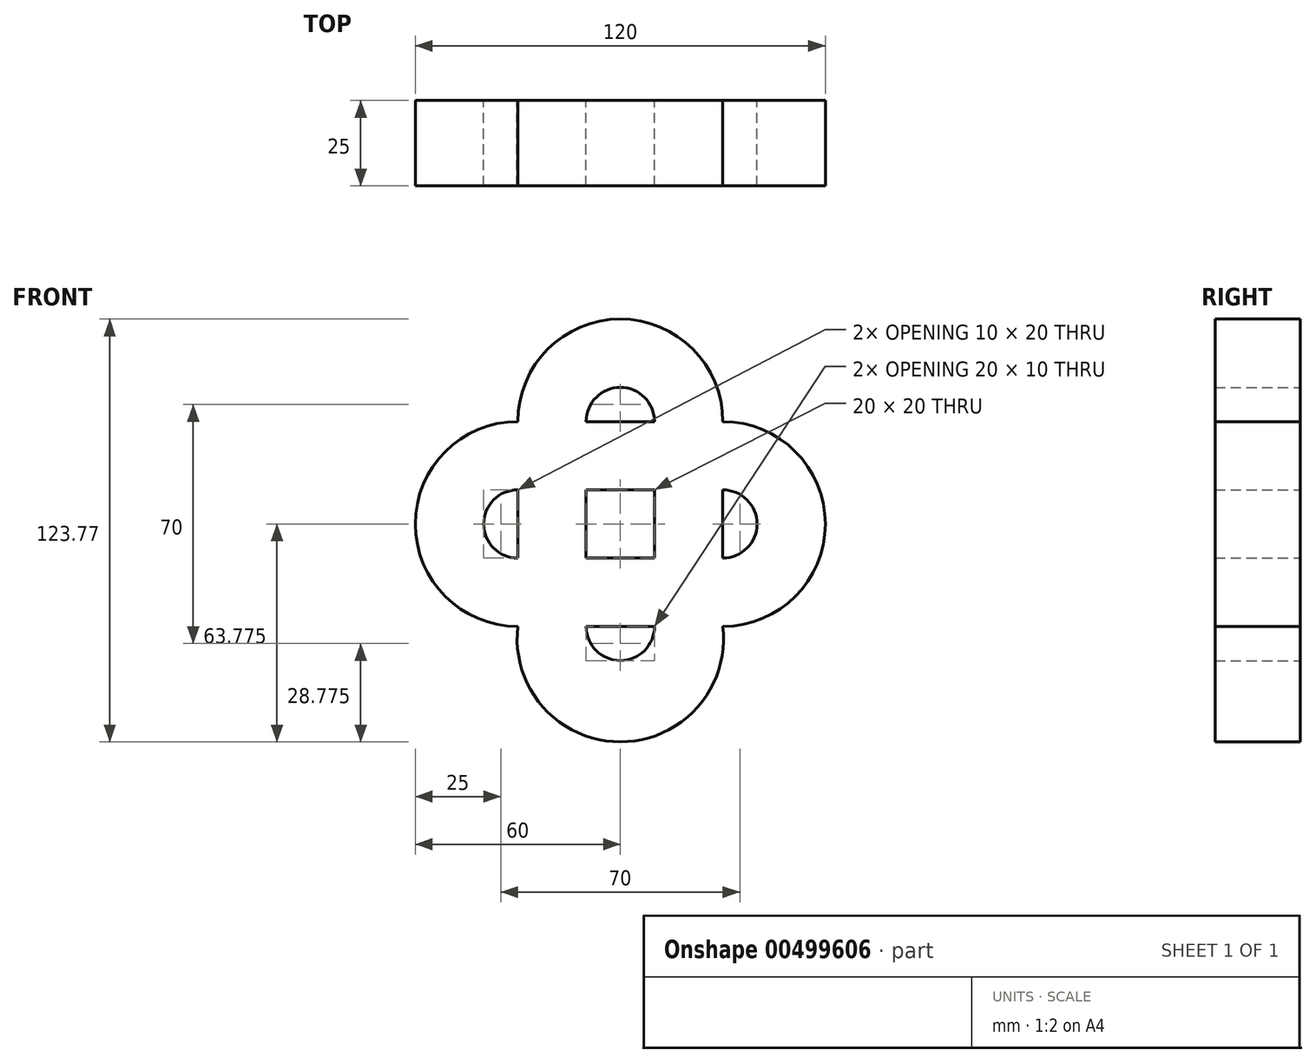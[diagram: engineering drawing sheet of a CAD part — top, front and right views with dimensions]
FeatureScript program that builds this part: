
annotation { "Feature Type Name" : "Feature", "Feature Type Description" : "" }
export const myFeature = defineFeature(function(context is Context, id is Id, definition is map)
    precondition{}
    {
        {
            var Q0;
            Q0=qCreatedBy(makeId("Front.planeOp"),FACE);
            var sketch = newSketch(context, id + "F0", { "sketchPlane" : qUnion([Q0])});
            skLineSegment(sketch, "E0.bottom", {"start": v(-20, 11.5) * mm, "end": v(0, 11.5) * mm});
            skLineSegment(sketch, "E0.top", {"start": v(-20, -8.5) * mm, "end": v(0, -8.5) * mm});
            skLineSegment(sketch, "E0.left", {"start": v(-20, 11.5) * mm, "end": v(-20, -8.5) * mm});
            skLineSegment(sketch, "E0.right", {"start": v(0, 11.5) * mm, "end": v(0, -8.5) * mm});
            skLineSegment(sketch, "E1", {"start": v(-20, 11.5) * mm, "end": v(-20, 31.5) * mm});
            skLineSegment(sketch, "E2", {"start": v(0, 11.5) * mm, "end": v(20, 11.5) * mm});
            skLineSegment(sketch, "E3", {"start": v(0, -8.5) * mm, "end": v(0, -28.5) * mm});
            skLineSegment(sketch, "E4", {"start": v(-20, -8.5) * mm, "end": v(-40, -8.5) * mm});
            skLineSegment(sketch, "E5", {"start": v(-20, 31.5) * mm, "end": v(20, 31.5) * mm});
            skLineSegment(sketch, "E6", {"start": v(20, 11.5) * mm, "end": v(20, -28.5) * mm});
            skLineSegment(sketch, "E7", {"start": v(0, -28.5) * mm, "end": v(-40, -28.5) * mm});
            skLineSegment(sketch, "E8", {"start": v(-40, -8.5) * mm, "end": v(-40, 31.5) * mm});
            skArc(sketch, "E9", {"start": v(20, 31.5) * mm, "mid": v(-10, 61.5) * mm, "end": v(-40, 31.5) * mm});
            skArc(sketch, "E10", {"start": v(20, -28.5) * mm, "mid": v(50, 1.5) * mm, "end": v(20, 31.5) * mm});
            skArc(sketch, "E11", {"start": v(-40, -28.5) * mm, "mid": v(-10, -62.27) * mm, "end": v(20, -28.5) * mm});
            skArc(sketch, "E12", {"start": v(-40, 31.5) * mm, "mid": v(-70, 1.5) * mm, "end": v(-40, -28.5) * mm});
            skArc(sketch, "E13", {"start": v(0, 31.5) * mm, "mid": v(-10, 41.5) * mm, "end": v(-20, 31.5) * mm});
            skArc(sketch, "E14", {"start": v(20, -8.5) * mm, "mid": v(30, 1.5) * mm, "end": v(20, 11.5) * mm});
            skArc(sketch, "E15", {"start": v(-20, -28.5) * mm, "mid": v(-10, -38.5) * mm, "end": v(0, -28.5) * mm});
            skArc(sketch, "E16", {"start": v(-40, 11.5) * mm, "mid": v(-50, 1.5) * mm, "end": v(-40, -8.5) * mm});
            skSolve(sketch);
        }
        {
            var Q0;
            Q0 = qSketchRegion(id + "F0", true);
            extrude(context, id + "F1", {"entities" : qUnion([Q0]), "depth" : 25 * mm});
        }
    });
